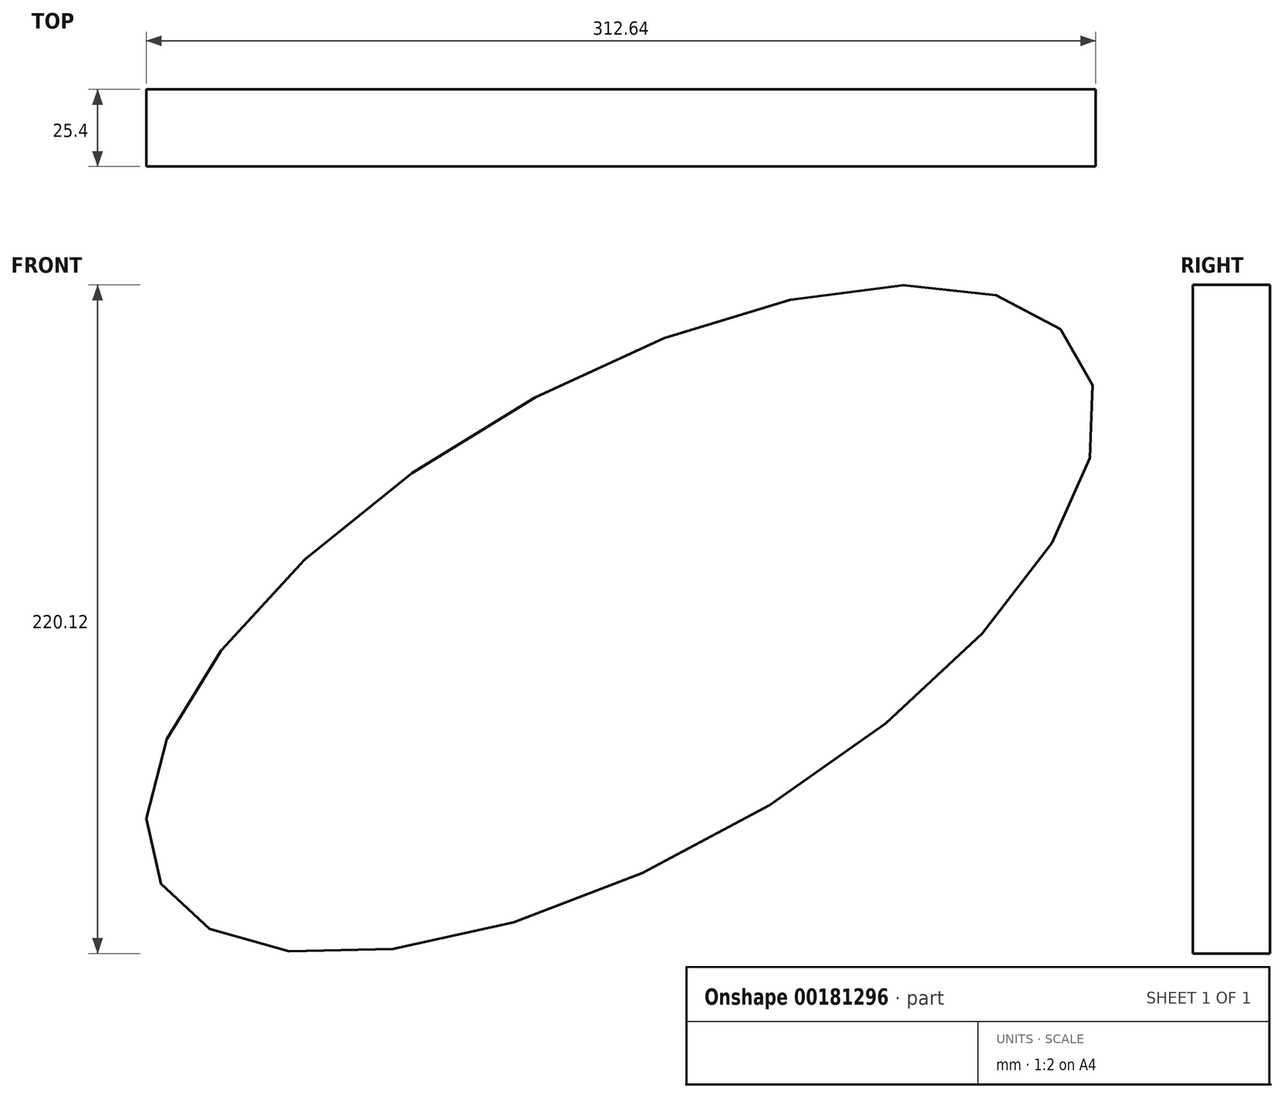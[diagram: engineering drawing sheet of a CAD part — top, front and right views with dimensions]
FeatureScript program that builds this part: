
annotation { "Feature Type Name" : "Feature", "Feature Type Description" : "" }
export const myFeature = defineFeature(function(context is Context, id is Id, definition is map)
    precondition{}
    {
        {
            var Q0;
            Q0=qCreatedBy(makeId("Front.planeOp"),FACE);
            var sketch = newSketch(context, id + "F0", { "sketchPlane" : qUnion([Q0])});
            skEllipse(sketch, "E0", {"center": v(160.1, 119.57) * mm, "majorRadius": 174.71 * mm, "minorRadius": 77.62 * mm, "majorAxis": v(-0.87, -0.5)});
            skSolve(sketch);
        }
        {
            var Q0;
            Q0 = qSketchRegion(id + "F0", true);
            extrude(context, id + "F1", {"entities" : qUnion([Q0]), "endBound" : BoundingType.SYMMETRIC, "depth" : 25.4 * mm});
        }
    });
